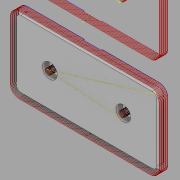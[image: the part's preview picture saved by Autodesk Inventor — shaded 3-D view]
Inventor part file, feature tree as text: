
AUTODESK INVENTOR PART (.ipt)
format: ipt  version: 2021.3 (Build 253353000, 353)  size: 150,016 bytes
history: native  units: in
note: dims shown in document units (in); Inventor stores cm internally (conversion verified against a paired STEP export)
features: sketch x2, other x1, extrude x1, hole x1, fillet x1, projected_geometry x1
ambient origin geometry x8: Origin, YZ Plane, XZ Plane, XY Plane, X Axis, Y Axis, Z Axis, Center Point
bodies: Body1 (feature_tree)
feature tree (7):
  other  "ソリッド1"
  extrude  "押し出し1"  Depth=2.4803in
  hole  "穴1"  [1 undecoded]
  fillet  "フィレット1"  Radius=0.5906in
  sketch  "スケッチ2"
  sketch  "スケッチ3"
  projected_geometry  "投影ループ1"
note: 1 required parameter value undecoded (feature->parameter linkage not recoverable at this tier; creation-order binding heuristic only, values carry confidence <= 0.55)
